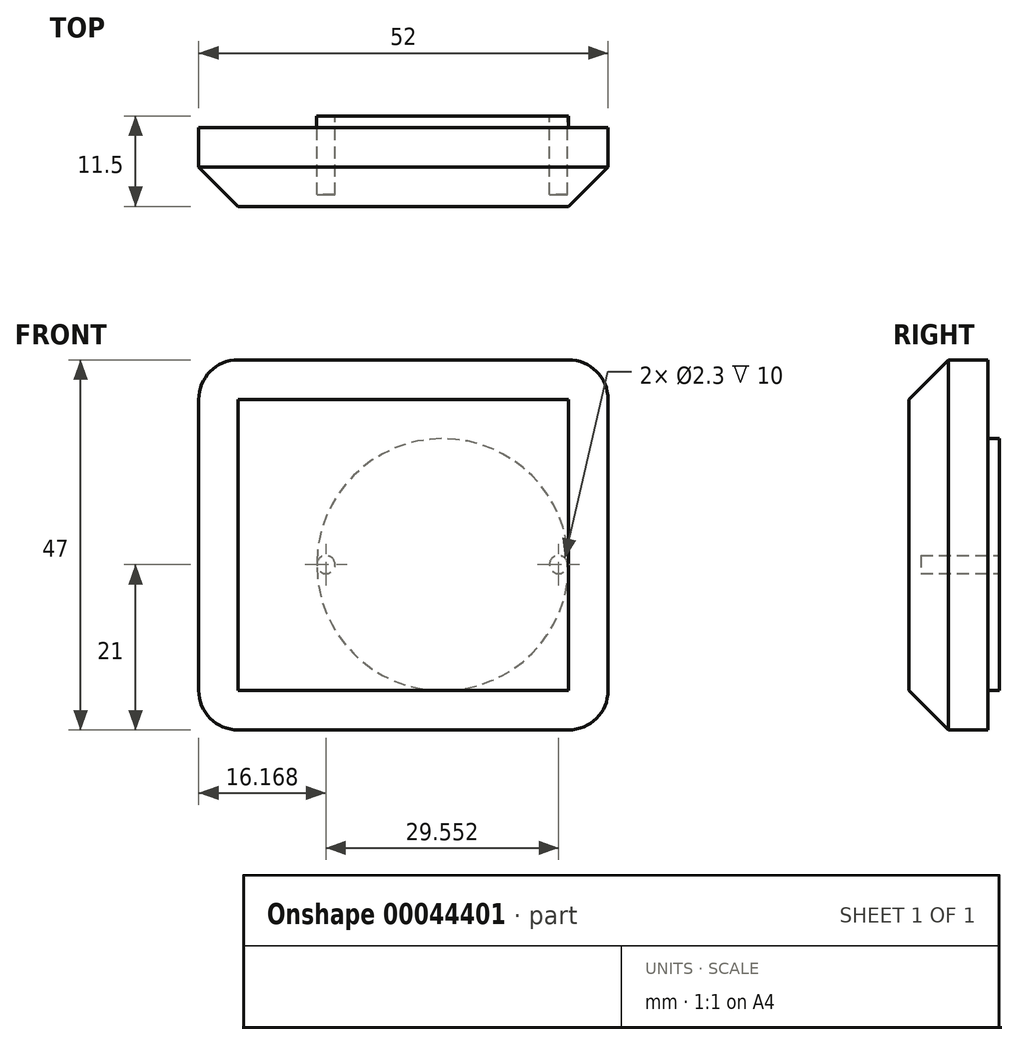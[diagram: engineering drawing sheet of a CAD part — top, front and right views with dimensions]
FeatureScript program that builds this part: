
annotation { "Feature Type Name" : "Feature", "Feature Type Description" : "" }
export const myFeature = defineFeature(function(context is Context, id is Id, definition is map)
    precondition{}
    {
        {
            var Q0;
            Q0=qCreatedBy(makeId("Front.planeOp"),FACE);
            var sketch = newSketch(context, id + "F0", { "sketchPlane" : qUnion([Q0])});
            skCircle(sketch, "E0", {"center": v(0, 0) * mm, "radius": 16 * mm});
            skSolve(sketch);
        }
        {
            var Q0;
            Q0=makeQuery(id+"F0.imprint","IMPRINT",FACE,{"disambiguationData":[TD([[makeQuery(id+"F0.imprint","IMPRINT",EDGE,{"derivedFrom":sQuery(id+"F0.wireOp",EDGE,"E0")}),1.0]])]});
            extrude(context, id + "F1", {"entities" : qUnion([Q0]), "oppositeDirection" : true, "depth" : 1.5 * mm});
        }
        {
            var Q0;
            Q0=qCreatedBy(makeId("Front.planeOp"),FACE);
            var sketch = newSketch(context, id + "F2", { "sketchPlane" : qUnion([Q0])});
            skLineSegment(sketch, "E1.bottom", {"start": v(-26, -21) * mm, "end": v(16, -21) * mm});
            skLineSegment(sketch, "E1.top", {"start": v(-26, 26) * mm, "end": v(16, 26) * mm});
            skLineSegment(sketch, "E1.left", {"start": v(-31, -16) * mm, "end": v(-31, 21) * mm});
            skLineSegment(sketch, "E1.right", {"start": v(21, -16) * mm, "end": v(21, 21) * mm});
            skPoint(sketch, "E2.visualSharp", {"position": v(-31, 26) * mm});
            skArc(sketch, "E2.filletArc", {"start": v(-26, 26) * mm, "mid": v(-29.54, 24.54) * mm, "end": v(-31, 21) * mm});
            skPoint(sketch, "E3.visualSharp", {"position": v(21, 26) * mm});
            skArc(sketch, "E3.filletArc", {"start": v(21, 21) * mm, "mid": v(19.54, 24.54) * mm, "end": v(16, 26) * mm});
            skPoint(sketch, "E4.visualSharp", {"position": v(21, -21) * mm});
            skArc(sketch, "E4.filletArc", {"start": v(16, -21) * mm, "mid": v(19.54, -19.54) * mm, "end": v(21, -16) * mm});
            skPoint(sketch, "E5.visualSharp", {"position": v(-31, -21) * mm});
            skArc(sketch, "E5.filletArc", {"start": v(-31, -16) * mm, "mid": v(-29.54, -19.54) * mm, "end": v(-26, -21) * mm});
            skSolve(sketch);
        }
        {
            var Q0;
            Q0=makeQuery(id+"F2.imprint","IMPRINT",FACE,{"disambiguationData":[TD([[makeQuery(id+"F2.imprint","IMPRINT",EDGE,{"derivedFrom":sQuery(id+"F2.wireOp",EDGE,"E1.bottom")}),1.0]])]});
            extrude(context, id + "F3", {"entities" : qUnion([Q0]), "operationType" : NewBodyOperationType.ADD, "depth" : 10 * mm});
        }
        {
            var Q0;
            Q0=makeQuery(id+"F3.opExtrude","CAP_FACE",FACE,{"disambiguationData":[OSD([sQuery(id+"F2.wireOp",EDGE,"E1.bottom"),sQuery(id+"F2.wireOp",EDGE,"E1.top"),sQuery(id+"F2.wireOp",EDGE,"E1.left"),sQuery(id+"F2.wireOp",EDGE,"E1.right"),sQuery(id+"F2.wireOp",EDGE,"E2.filletArc"),sQuery(id+"F2.wireOp",EDGE,"E3.filletArc"),sQuery(id+"F2.wireOp",EDGE,"E4.filletArc"),sQuery(id+"F2.wireOp",EDGE,"E5.filletArc")])],"isStart":false});
            chamfer(context, id + "F4", {"entities" : qUnion([Q0]), "width" : 5 * mm, "tangentPropagation" : true});
        }
        {
            var Q0;
            Q0=makeQuery(id+"F1.opExtrude","CAP_FACE",FACE,{"disambiguationData":[OSD([sQuery(id+"F0.wireOp",EDGE,"E0")])],"isStart":false});
            var sketch = newSketch(context, id + "F5", { "sketchPlane" : qUnion([Q0])});
            skCircle(sketch, "E6", {"center": v(14.83, 0) * mm, "radius": 1.15 * mm});
            skCircle(sketch, "E7", {"center": v(-14.72, 0) * mm, "radius": 1.15 * mm});
            skSolve(sketch);
        }
        {
            var Q0;
            Q0=makeQuery(id+"F5.imprint","IMPRINT",FACE,{"disambiguationData":[TD([[makeQuery(id+"F5.imprint","IMPRINT",EDGE,{"derivedFrom":sQuery(id+"F5.wireOp",EDGE,"E6")}),1.0]])]});
            var Q1;
            Q1=makeQuery(id+"F5.imprint","IMPRINT",FACE,{"disambiguationData":[TD([[makeQuery(id+"F5.imprint","IMPRINT",EDGE,{"derivedFrom":sQuery(id+"F5.wireOp",EDGE,"E7")}),1.0]])]});
            extrude(context, id + "F6", {"entities" : qUnion([Q0, Q1]), "operationType" : NewBodyOperationType.REMOVE, "oppositeDirection" : true, "depth" : 10 * mm});
        }
    });
